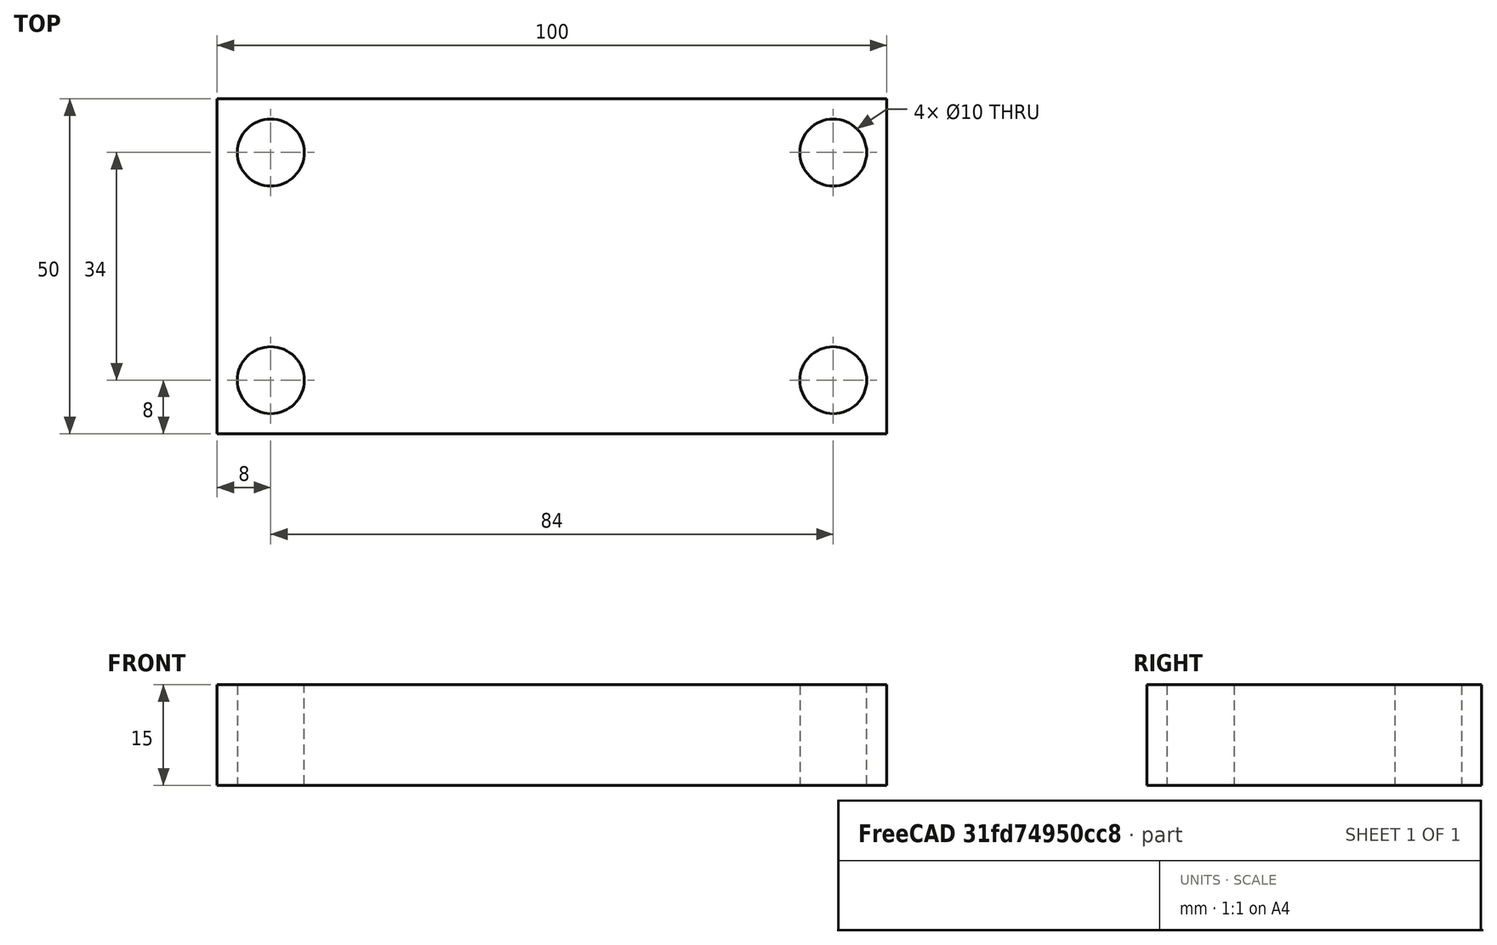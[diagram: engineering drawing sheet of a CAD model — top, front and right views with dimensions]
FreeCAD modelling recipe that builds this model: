
FCSTD DOCUMENT  (FreeCAD 0.20R29177 +426 (Git))
Label: 097_prbl1
License: All rights reserved
LicenseURL: http://en.wikipedia.org/wiki/All_rights_reserved
objects: TechDraw::DrawViewDimension×11, TechDraw::DrawViewAnnotation×7, TechDraw::DrawViewPart×5, Sketcher::SketchObject×2, PartDesign::Pad×2, PartDesign::Body×2, TechDraw::DrawSVGTemplate×2, TechDraw::DrawPage×2
note: 8 computed .brp shape members not serialized (recipe doc carries the construction recipe); baked Part::Feature solids carry a one-line shape summary decoded from their .brp

FEATURE [Sketcher::SketchObject] Sketch001
  FullyConstrained = true
  MapMode = 5
  Support = -> [XY_Plane]
  sketch-geometry (8):
    g0: LineSegment StartX=0 StartY=50 StartZ=0 EndX=100 EndY=50 EndZ=0
    g1: LineSegment StartX=100 StartY=50 StartZ=0 EndX=100 EndY=0 EndZ=0
    g2: LineSegment StartX=100 StartY=0 StartZ=0 EndX=0 EndY=0 EndZ=0
    g3: LineSegment StartX=0 StartY=0 StartZ=0 EndX=0 EndY=50 EndZ=0
    g4: Circle CenterX=92 CenterY=42 CenterZ=0 NormalX=0 NormalY=0 NormalZ=1 AngleXU=0 Radius=5
    g5: Circle CenterX=8 CenterY=42 CenterZ=0 NormalX=0 NormalY=0 NormalZ=1 AngleXU=0 Radius=5
    g6: Circle CenterX=92 CenterY=8 CenterZ=0 NormalX=0 NormalY=0 NormalZ=1 AngleXU=0 Radius=5
    g7: Circle CenterX=8 CenterY=8 CenterZ=0 NormalX=0 NormalY=0 NormalZ=1 AngleXU=0 Radius=5
  constraints (24):
    c: Coincident(g0,g1)
    c: Coincident(g1,g2)
    c: Coincident(g2,g3)
    c: Coincident(g3,g0)
    c: Horizontal(g0)
    c: Horizontal(g2)
    c: Vertical(g1)
    c: Vertical(g3)
    c: DistanceY(g1,g1) = 50
    c: DistanceX(g0,g0) = 100
    c: Radius(g4) = 5
    c: Radius(g7) = 5
    c: Radius(g5) = 5
    c: Radius(g6) = 5
    c: DistanceX(g2,g7) = 8
    c: DistanceX(g0,g5) = 8
    c: DistanceX(g4,g0) = 8
    c: DistanceX(g6,g1) = 8
    c: DistanceY(g5,g0) = 8
    c: DistanceY(g4,g0) = 8
    c: DistanceY(g1,g6) = 8
    c: DistanceY(g2,g7) = 8
    c: DistanceX(g-1,g2) = 0
    c: DistanceY(g-1,g2) = 0
FEATURE [PartDesign::Pad] Pad
  Direction = (0,0,1)
  Length = 15
  Length2 = 10
  Profile = -> Sketch001
  ReferenceAxis = -> Sketch001 [N_Axis]
  Type = 0
FEATURE [PartDesign::Pad] Pad001
  BaseFeature = -> Pad
  Direction = (0,0,1)
  Length = 15
  Length2 = 10
  Profile = -> Sketch001
  ReferenceAxis = -> Sketch001 [N_Axis]
  Type = 0
FEATURE [PartDesign::Body] Body
  Group = -> [Sketch001,Pad,Pad001]
  Origin = -> Origin
  Tip = -> Pad001
FEATURE [TechDraw::DrawSVGTemplate] Template
  EditableTexts = APPROVER_NAME=KEYUR SURATI; AUTHOR_NAME=MANSI RAJPUT(231); DATE=2023-04-20; DN=8; DOCUMENT_TYPE=PART DESIGN; OWNER_NAME=AMTICS; SCALE=1:1; SHEET=8; SIZE=A4; TITLELINE-1=ORTHOGRAPHIC VIEW OF FOUNDATION PLATE
  Height = 210
  Orientation = 1
  Width = 297
FEATURE [TechDraw::DrawViewPart] View
  CoarseView = false
  Direction = (0.577,-0.577,0.577)
  Focus = 100
  HardHidden = false
  IsoCount = 0
  IsoHidden = false
  IsoVisible = false
  LockPosition = false
  Perspective = false
  Rotation = 0
  ScaleType = 0
  SeamHidden = false
  SeamVisible = true
  SmoothHidden = false
  SmoothVisible = true
  Source = -> [Pad001]
  X = 72.6871
  XDirection = (0.707,0.707,0)
  Y = 75.1108
FEATURE [TechDraw::DrawViewPart] View001
  CoarseView = false
  Direction = (0,-1,0)
  Focus = 100
  HardHidden = false
  IsoCount = 0
  IsoHidden = false
  IsoVisible = false
  LockPosition = false
  Perspective = false
  Rotation = 0
  ScaleType = 0
  SeamHidden = false
  SeamVisible = true
  SmoothHidden = false
  SmoothVisible = true
  Source = -> [Pad001]
  X = 233.831
  XDirection = (1,0,0)
  Y = 172.865
FEATURE [TechDraw::DrawViewPart] View002
  CoarseView = false
  Direction = (0,0,1)
  Focus = 100
  HardHidden = false
  IsoCount = 0
  IsoHidden = false
  IsoVisible = false
  LockPosition = false
  Perspective = false
  Rotation = 0
  ScaleType = 0
  SeamHidden = false
  SeamVisible = true
  SmoothHidden = false
  SmoothVisible = true
  Source = -> [Pad001]
  X = 233.415
  XDirection = (1,0,0)
  Y = 107.495
FEATURE [TechDraw::DrawViewPart] View003
  CoarseView = false
  Direction = (1,0,0)
  Focus = 100
  HardHidden = false
  IsoCount = 0
  IsoHidden = false
  IsoVisible = false
  LockPosition = false
  Perspective = false
  Rotation = 0
  ScaleType = 0
  SeamHidden = false
  SeamVisible = true
  SmoothHidden = false
  SmoothVisible = true
  Source = -> [Pad001]
  X = 118.054
  XDirection = (0,1,0)
  Y = 174.051
FEATURE [TechDraw::DrawViewAnnotation] Annotation
  Font = osifont
  LineSpace = 80
  LockPosition = false
  MaxWidth = -1
  Rotation = 0
  ScaleType = 0
  Text = RHSV
  TextSize = 5
  TextStyle = 0
  X = 118.543
  Y = 186.208
FEATURE [TechDraw::DrawViewAnnotation] Annotation001
  Font = osifont
  LineSpace = 80
  LockPosition = false
  MaxWidth = -1
  Rotation = 0
  ScaleType = 0
  Text = FV
  TextSize = 5
  TextStyle = 0
  X = 232.334
  Y = 185.341
FEATURE [TechDraw::DrawViewAnnotation] Annotation002
  Font = osifont
  LineSpace = 80
  LockPosition = false
  MaxWidth = -1
  Rotation = 0
  ScaleType = 0
  Text = ISOMETRIC VIEW
  TextSize = 5
  TextStyle = 0
  X = 73.0191
  Y = 20.2326
FEATURE [TechDraw::DrawViewAnnotation] Annotation003
  Font = osifont
  LineSpace = 80
  LockPosition = false
  MaxWidth = -1
  Rotation = 0
  ScaleType = 0
  Text = TV
  TextSize = 5
  TextStyle = 0
  X = 232.167
  Y = 64.9129
FEATURE [TechDraw::DrawViewAnnotation] Annotation004
  Font = osifont
  LineSpace = 80
  LockPosition = false
  MaxWidth = -1
  Rotation = 0
  ScaleType = 0
  Text = ##: ALL THE DIMENSIONS ARE IN mm.
  TextSize = 5
  TextStyle = 0
  X = 190.94
  Y = 42.8818
FEATURE [TechDraw::DrawViewDimension] Dimension
  AngleOverride = false
  Arbitrary = false
  ArbitraryTolerances = false
  EqualTolerance = true
  ExtensionAngle = 0
  FormatSpec = %.2w
  FormatSpecOverTolerance = %+.2w
  FormatSpecUnderTolerance = %+.2w
  Inverted = false
  LineAngle = 0
  LockPosition = false
  MeasureType = 1
  OverTolerance = 0
  References2D = -> [View003]
  Rotation = 0
  ScaleType = 0
  TheoreticalExact = false
  Type = 2
  UnderTolerance = 0
  X = -32.3813
  Y = 0.918294
FEATURE [TechDraw::DrawViewDimension] Dimension001
  AngleOverride = false
  Arbitrary = false
  ArbitraryTolerances = false
  EqualTolerance = true
  ExtensionAngle = 0
  FormatSpec = %.2w
  FormatSpecOverTolerance = %+.2w
  FormatSpecUnderTolerance = %+.2w
  Inverted = false
  LineAngle = 0
  LockPosition = false
  MeasureType = 1
  OverTolerance = 0
  References2D = -> [View003]
  Rotation = 0
  ScaleType = 0
  TheoreticalExact = false
  Type = 1
  UnderTolerance = 0
  X = -0.263618
  Y = -10.2724
FEATURE [TechDraw::DrawViewDimension] Dimension003
  AngleOverride = false
  Arbitrary = false
  ArbitraryTolerances = false
  EqualTolerance = true
  ExtensionAngle = 0
  FormatSpec = %.2w
  FormatSpecOverTolerance = %+.2w
  FormatSpecUnderTolerance = %+.2w
  Inverted = false
  LineAngle = 0
  LockPosition = false
  MeasureType = 1
  OverTolerance = 0
  References2D = -> [View001]
  Rotation = 0
  ScaleType = 0
  TheoreticalExact = false
  Type = 1
  UnderTolerance = 0
  X = -1.05447
  Y = -9.74512
FEATURE [TechDraw::DrawViewDimension] Dimension004
  AngleOverride = false
  Arbitrary = false
  ArbitraryTolerances = false
  EqualTolerance = true
  ExtensionAngle = 0
  FormatSpec = %.2w
  FormatSpecOverTolerance = %+.2w
  FormatSpecUnderTolerance = %+.2w
  Inverted = false
  LineAngle = 0
  LockPosition = false
  MeasureType = 1
  OverTolerance = 0
  References2D = -> [View002]
  Rotation = 0
  ScaleType = 0
  TheoreticalExact = false
  Type = 1
  UnderTolerance = 0
  X = -1.05447
  Y = 33.8268
FEATURE [TechDraw::DrawViewDimension] Dimension005
  AngleOverride = false
  Arbitrary = false
  ArbitraryTolerances = false
  EqualTolerance = true
  ExtensionAngle = 0
  FormatSpec = %.2w
  FormatSpecOverTolerance = %+.2w
  FormatSpecUnderTolerance = %+.2w
  Inverted = false
  LineAngle = 0
  LockPosition = false
  MeasureType = 1
  OverTolerance = 0
  References2D = -> [View002]
  Rotation = 0
  ScaleType = 0
  TheoreticalExact = false
  Type = 2
  UnderTolerance = 0
  X = -68.1896
  Y = 1.97276
FEATURE [TechDraw::DrawViewDimension] Dimension006
  AngleOverride = false
  Arbitrary = false
  ArbitraryTolerances = false
  EqualTolerance = true
  ExtensionAngle = 0
  FormatSpec = ⌀%.2w
  FormatSpecOverTolerance = %+.2w
  FormatSpecUnderTolerance = %+.2w
  Inverted = false
  LineAngle = 0
  LockPosition = false
  MeasureType = 1
  OverTolerance = 0
  References2D = -> [View002]
  Rotation = 0
  ScaleType = 0
  TheoreticalExact = false
  Type = 5
  UnderTolerance = 0
  X = -58.5231
  Y = 13.4445
FEATURE [TechDraw::DrawViewDimension] Dimension007
  AngleOverride = false
  Arbitrary = false
  ArbitraryTolerances = false
  EqualTolerance = true
  ExtensionAngle = 0
  FormatSpec = %.2w
  FormatSpecOverTolerance = %+.2w
  FormatSpecUnderTolerance = %+.2w
  Inverted = false
  LineAngle = 0
  LockPosition = false
  MeasureType = 1
  OverTolerance = 0
  References2D = -> [View001]
  Rotation = 0
  ScaleType = 0
  TheoreticalExact = false
  Type = 2
  UnderTolerance = 0
  X = -55.2724
  Y = 1.44553
FEATURE [TechDraw::DrawPage] Page
  KeepUpdated = true
  NextBalloonIndex = 1
  ProjectionType = 0
  Template = -> Template
  Views = -> [View,View001,View002,View003,Annotation,Annotation001,Annotation002,Annotation003,Annotation004,Dimension,Dimension001,Dimension003,Dimension004,Dimension005,Dimension006,Dimension007]
FEATURE [TechDraw::DrawSVGTemplate] Template001
  EditableTexts = APPROVER_NAME=KEYUR SURATI; AUTHOR_NAME=KRISH B.(099); DATE=2023-04-20; DN=9; DOCUMENT_TYPE=PART DESIGN; OWNER_NAME=AMTICS; SCALE=1:1.70; SHEET=9; SIZE=A4; TITLELINE-1=ISOMETRIC VIEW OF FOUNDATION PLATE
  Height = 210
  Orientation = 1
  Width = 297
FEATURE [TechDraw::DrawViewPart] View004
  CoarseView = false
  Direction = (0.577,-0.577,0.577)
  Focus = 100
  HardHidden = false
  IsoCount = 0
  IsoHidden = false
  IsoVisible = false
  LockPosition = false
  Perspective = false
  Rotation = 0
  Scale = 1.7
  ScaleType = 0
  SeamHidden = false
  SeamVisible = true
  SmoothHidden = false
  SmoothVisible = true
  Source = -> [Pad001]
  X = 157.81
  XDirection = (0.707,0.707,0)
  Y = 124.889
FEATURE [TechDraw::DrawViewAnnotation] Annotation005
  Font = osifont
  LineSpace = 80
  LockPosition = false
  MaxWidth = -1
  Rotation = 0
  Scale = 1.7
  ScaleType = 0
  Text = ISOMETRIC VIEW
  TextSize = 5
  TextStyle = 0
  X = 84.4929
  Y = 83.5423
FEATURE [TechDraw::DrawViewDimension] Dimension008
  AngleOverride = false
  Arbitrary = false
  ArbitraryTolerances = false
  EqualTolerance = true
  ExtensionAngle = 0
  FormatSpec = %.2w
  FormatSpecOverTolerance = %+.2w
  FormatSpecUnderTolerance = %+.2w
  Inverted = false
  LineAngle = 0
  LockPosition = false
  MeasureType = 1
  OverTolerance = 0
  References2D = -> [View004]
  Rotation = 0
  Scale = 1.7
  ScaleType = 0
  TheoreticalExact = false
  Type = 0
  UnderTolerance = 0
  X = 42.9939
  Y = 31.825
FEATURE [TechDraw::DrawViewDimension] Dimension009
  AngleOverride = false
  Arbitrary = false
  ArbitraryTolerances = false
  EqualTolerance = true
  ExtensionAngle = 0
  FormatSpec = %.2w
  FormatSpecOverTolerance = %+.2w
  FormatSpecUnderTolerance = %+.2w
  Inverted = false
  LineAngle = 0
  LockPosition = false
  MeasureType = 1
  OverTolerance = 0
  References2D = -> [View004]
  Rotation = 0
  Scale = 1.7
  ScaleType = 0
  TheoreticalExact = false
  Type = 2
  UnderTolerance = 0
  X = -108.883
  Y = 17.8715
FEATURE [TechDraw::DrawViewDimension] Dimension010
  AngleOverride = false
  Arbitrary = false
  ArbitraryTolerances = false
  EqualTolerance = true
  ExtensionAngle = 0
  FormatSpec = R%.2w
  FormatSpecOverTolerance = %+.2w
  FormatSpecUnderTolerance = %+.2w
  Inverted = false
  LineAngle = 0
  LockPosition = false
  MeasureType = 1
  OverTolerance = 0
  References2D = -> [View004]
  Rotation = 0
  Scale = 1.7
  ScaleType = 0
  TheoreticalExact = false
  Type = 4
  UnderTolerance = 0
  X = -105.017
  Y = 42.4752
FEATURE [TechDraw::DrawViewDimension] Dimension011
  AngleOverride = false
  Arbitrary = false
  ArbitraryTolerances = false
  EqualTolerance = true
  ExtensionAngle = 0
  FormatSpec = %.2w
  FormatSpecOverTolerance = %+.2w
  FormatSpecUnderTolerance = %+.2w
  Inverted = false
  LineAngle = 0
  LockPosition = false
  MeasureType = 1
  OverTolerance = 0
  References2D = -> [View004]
  Rotation = 0
  Scale = 1.7
  ScaleType = 0
  TheoreticalExact = false
  Type = 0
  UnderTolerance = 0
  X = 60.7217
  Y = -47.6698
FEATURE [TechDraw::DrawViewAnnotation] Annotation006
  Font = osifont
  LineSpace = 80
  LockPosition = false
  MaxWidth = -1
  Rotation = 0
  Scale = 1.7
  ScaleType = 0
  Text = ##: ALL DIMENSIONS ARE IN mm.
  TextSize = 5
  TextStyle = 0
  X = 186.153
  Y = 42.6215
FEATURE [TechDraw::DrawPage] Page001
  KeepUpdated = true
  NextBalloonIndex = 1
  ProjectionType = 0
  Scale = 1.7
  Template = -> Template001
  Views = -> [View004,Annotation005,Dimension008,Dimension009,Dimension010,Dimension011,Annotation006]
FEATURE [Sketcher::SketchObject] Sketch
  FullyConstrained = true
  MapMode = 5
  Support = -> [XY_Plane001]
FEATURE [PartDesign::Body] Body001
  Group = -> [Sketch]
  Origin = -> Origin001
